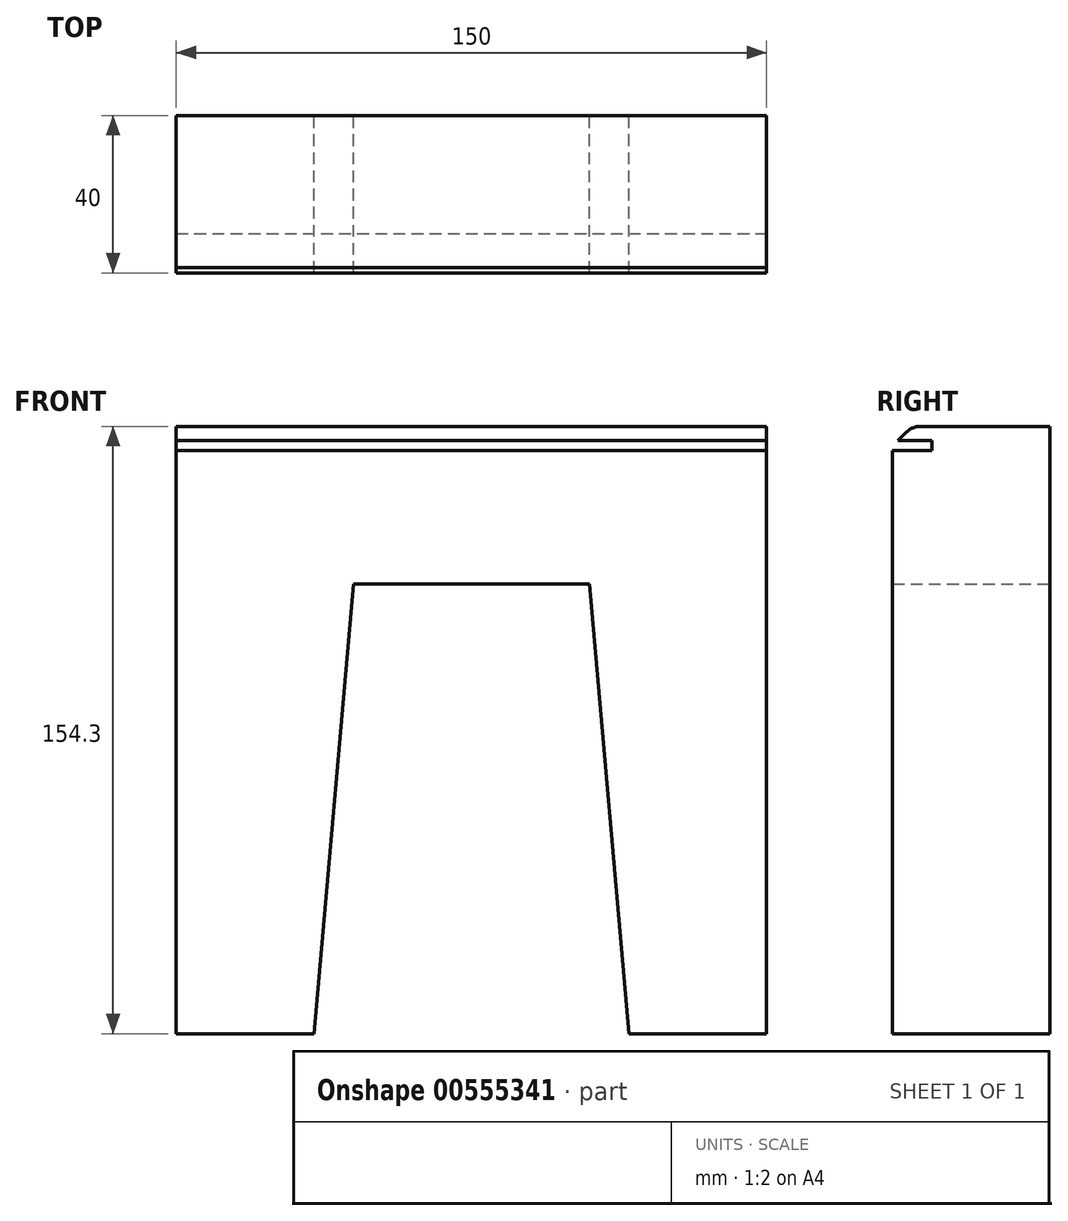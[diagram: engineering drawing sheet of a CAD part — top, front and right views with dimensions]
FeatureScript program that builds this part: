
annotation { "Feature Type Name" : "Feature", "Feature Type Description" : "" }
export const myFeature = defineFeature(function(context is Context, id is Id, definition is map)
    precondition{}
    {
        {
            var Q0;
            Q0=qCreatedBy(makeId("Front.planeOp"),FACE);
            var sketch = newSketch(context, id + "F0", { "sketchPlane" : qUnion([Q0])});
            skLineSegment(sketch, "E0", {"start": v(0, 0) * mm, "end": v(150, 0) * mm});
            skLineSegment(sketch, "E1", {"start": v(150, 0) * mm, "end": v(150, -154.3) * mm});
            skLineSegment(sketch, "E2", {"start": v(150, -154.3) * mm, "end": v(115, -154.3) * mm});
            skLineSegment(sketch, "E3", {"start": v(115, -154.3) * mm, "end": v(105, -40) * mm});
            skLineSegment(sketch, "E4", {"start": v(105, -40) * mm, "end": v(45, -40) * mm});
            skLineSegment(sketch, "E5", {"start": v(45, -40) * mm, "end": v(35, -154.3) * mm});
            skLineSegment(sketch, "E6", {"start": v(35, -154.3) * mm, "end": v(0, -154.3) * mm});
            skLineSegment(sketch, "E7", {"start": v(0, -154.3) * mm, "end": v(0, 0) * mm});
            skSolve(sketch);
        }
        {
            var Q0;
            Q0 = qSketchRegion(id + "F0", true);
            extrude(context, id + "F1", {"entities" : qUnion([Q0]), "depth" : 40 * mm, "offsetDistance" : 25 * mm});
        }
        {
            var Q0;
            Q0=makeQuery(id+"F1.opExtrude","CAP_FACE",FACE,{"disambiguationData":[OSD([sQuery(id+"F0.wireOp",EDGE,"E0"),sQuery(id+"F0.wireOp",EDGE,"E1"),sQuery(id+"F0.wireOp",EDGE,"E2"),sQuery(id+"F0.wireOp",EDGE,"E3"),sQuery(id+"F0.wireOp",EDGE,"E4"),sQuery(id+"F0.wireOp",EDGE,"E5"),sQuery(id+"F0.wireOp",EDGE,"E6"),sQuery(id+"F0.wireOp",EDGE,"E7")])],"isStart":false});
            var sketch = newSketch(context, id + "F2", { "sketchPlane" : qUnion([Q0])});
            skLineSegment(sketch, "E8.bottom", {"start": v(0, -3.64) * mm, "end": v(150, -3.64) * mm});
            skLineSegment(sketch, "E8.top", {"start": v(0, -6.14) * mm, "end": v(150, -6.14) * mm});
            skLineSegment(sketch, "E8.left", {"start": v(0, -3.64) * mm, "end": v(0, -6.14) * mm});
            skLineSegment(sketch, "E8.right", {"start": v(150, -3.64) * mm, "end": v(150, -6.14) * mm});
            skSolve(sketch);
        }
        {
            var Q0;
            Q0 = qSketchRegion(id + "F2", true);
            extrude(context, id + "F3", {"entities" : qUnion([Q0]), "operationType" : NewBodyOperationType.REMOVE, "oppositeDirection" : true, "depth" : 10 * mm, "offsetDistance" : 25 * mm});
        }
        {
            var Q0;
            Q0=makeQuery(id+"F1.opExtrude","CAP_EDGE",EDGE,{"disambiguationData":[OSD([sQuery(id+"F0.wireOp",EDGE,"E0")])],"isStart":false});
            chamfer(context, id + "F4", {"entities" : qUnion([Q0]), "width" : 5 * mm, "tangentPropagation" : true});
        }
        {
            var Q0;
            {var subQ0=sQuery(id+"F0.wireOp",EDGE,"E0");Q0=makeQuery(id+"F4.opChamfer","BLEND_EDGE",EDGE,{"blendedFrom":[makeQuery(id+"F1.opExtrude","CAP_EDGE",EDGE,{"disambiguationData":[OSD([subQ0])],"isStart":false}),makeQuery(id+"F1.opExtrude","SWEPT_FACE",FACE,{"disambiguationData":[OSD([subQ0])]})],"blendedInto":[makeQuery(id+"F1.opExtrude","SWEPT_FACE",FACE,{"disambiguationData":[OSD([subQ0])]})]});}
            fillet(context, id + "F5", {"entities" : qUnion([Q0]), "radius" : 5 * mm, "tangentPropagation" : true, "allowEdgeOverflow" : false});
        }
    });
